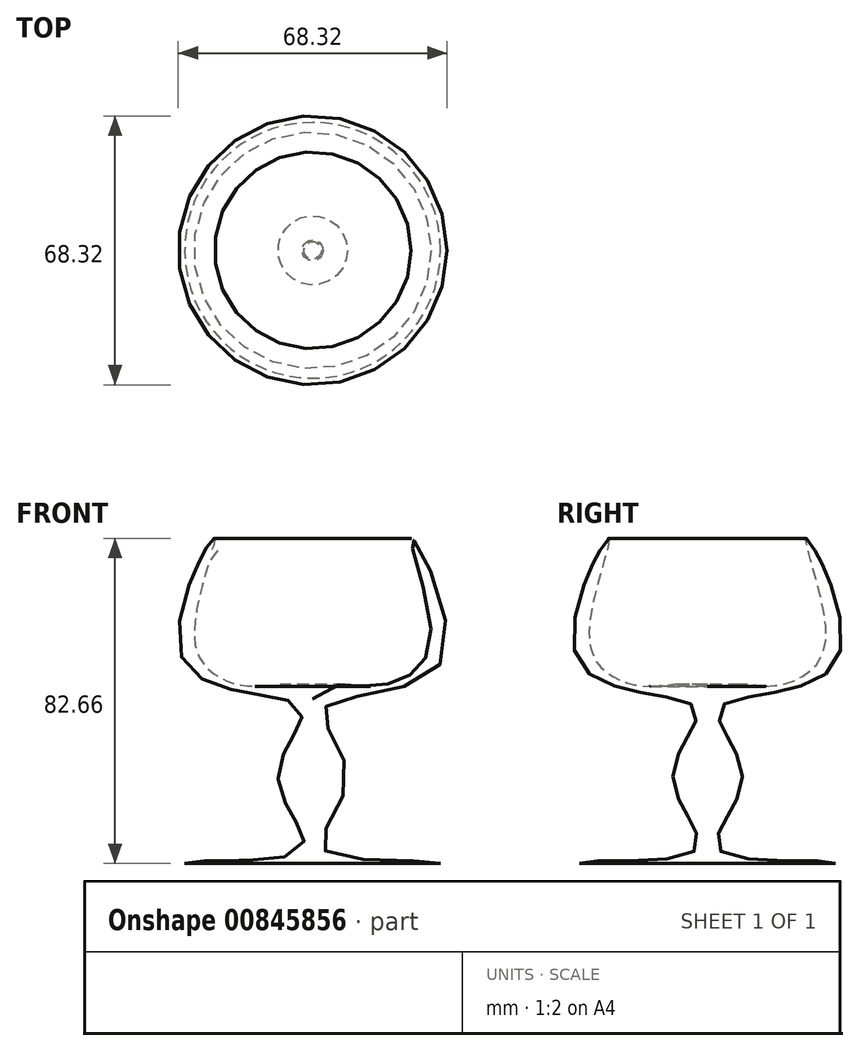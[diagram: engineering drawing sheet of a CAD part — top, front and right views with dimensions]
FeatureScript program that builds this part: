
annotation { "Feature Type Name" : "Feature", "Feature Type Description" : "" }
export const myFeature = defineFeature(function(context is Context, id is Id, definition is map)
    precondition{}
    {
        {
            var Q0;
            Q0=qCreatedBy(makeId("Front.planeOp"),FACE);
            var sketch = newSketch(context, id + "F0", { "sketchPlane" : qUnion([Q0])});
            skFitSpline(sketch, "E0", {"points": [v(32.5, 0) * mm, v(-4.1, -1.02) * mm, v(0.59, 42.43) * mm, v(13.99, 45.09) * mm, v(24.83, 48.01) * mm, v(30.03, 60.26) * mm, v(25.17, 82.65) * mm, v(32.8, 51.36) * mm, v(3.05, 39.58) * mm, v(8.8, 21.71) * mm, v(3.05, 3.38) * mm, v(32.5, 0) * mm]});
            skLineSegment(sketch, "E1", {"start": v(0, 64.24) * mm, "end": v(0, -28.72) * mm});
            skLineSegment(sketch, "E2", {"start": v(-15.4, 0) * mm, "end": v(36.7, 0) * mm});
            skSolve(sketch);
        }
        {
            var Q0;
            {var subQ0=sQuery(id+"F0.wireOp",EDGE,"E2");var subQ1=sQuery(id+"F0.wireOp",EDGE,"E0");var subQ2=makeQuery(id+"F0.imprint","INTERSECT",VERTEX,{"disambiguationData":[OD(0.0)],"derivedFrom":[subQ1,subQ0]});Q0=makeQuery(id+"F0.imprint","IMPRINT",FACE,{"disambiguationData":[TD([[makeQuery(id+"F0.imprint","IMPRINT",EDGE,{"disambiguationData":[TD([[subQ2,1.0]])],"derivedFrom":subQ1}),-1.0]])]});}
            var Q1;
            Q1=sQuery(id+"F0.wireOp",EDGE,"E1");
            revolve(context, id + "F1", {"surfaceOperationType" : NewSurfaceOperationType.NEW, "entities" : qUnion([Q0]), "axis" : qUnion([Q1]), "revolveType" : RevolveType.FULL});
        }
    });
